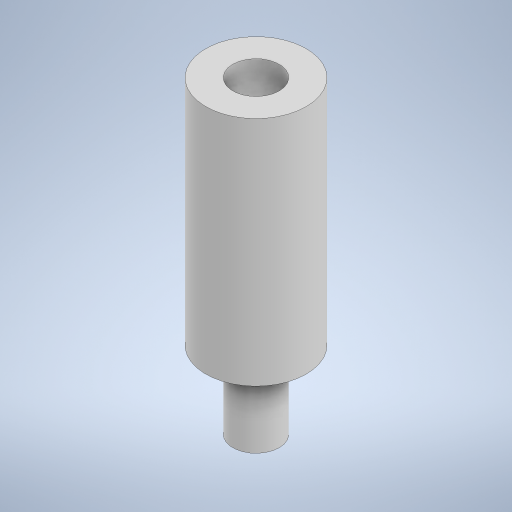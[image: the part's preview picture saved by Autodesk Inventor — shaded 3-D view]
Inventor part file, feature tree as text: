
AUTODESK INVENTOR PART (.ipt)
format: ipt  version: 2024.2 (Build 282272000, 272)  size: 235,008 bytes
history: native  units: mm
features: extrude x3, sketch x3
ambient origin geometry x8: Origin, YZ Plane, XZ Plane, XY Plane, X Axis, Y Axis, Z Axis, Center Point
bodies: Solid1 (feature_tree)
feature tree (6):
  extrude  "Extrusion1"  Depth=5.0mm TaperAngle=0.0deg
  extrude  "Extrusion2"  Depth=15.0mm TaperAngle=0.0deg
  extrude  "Extrusion3"  Depth=2.5mm TaperAngle=0.0deg
  sketch  "Sketch1"  dims[d0=3.0mm d1=5.0mm d2=0.0mm]
  sketch  "Sketch2"  dims[d3=6.5mm d4=15.0mm d5=0.0mm]
  sketch  "Sketch3"  dims[d6=3.2mm d7=2.5mm d8=0.0mm]
